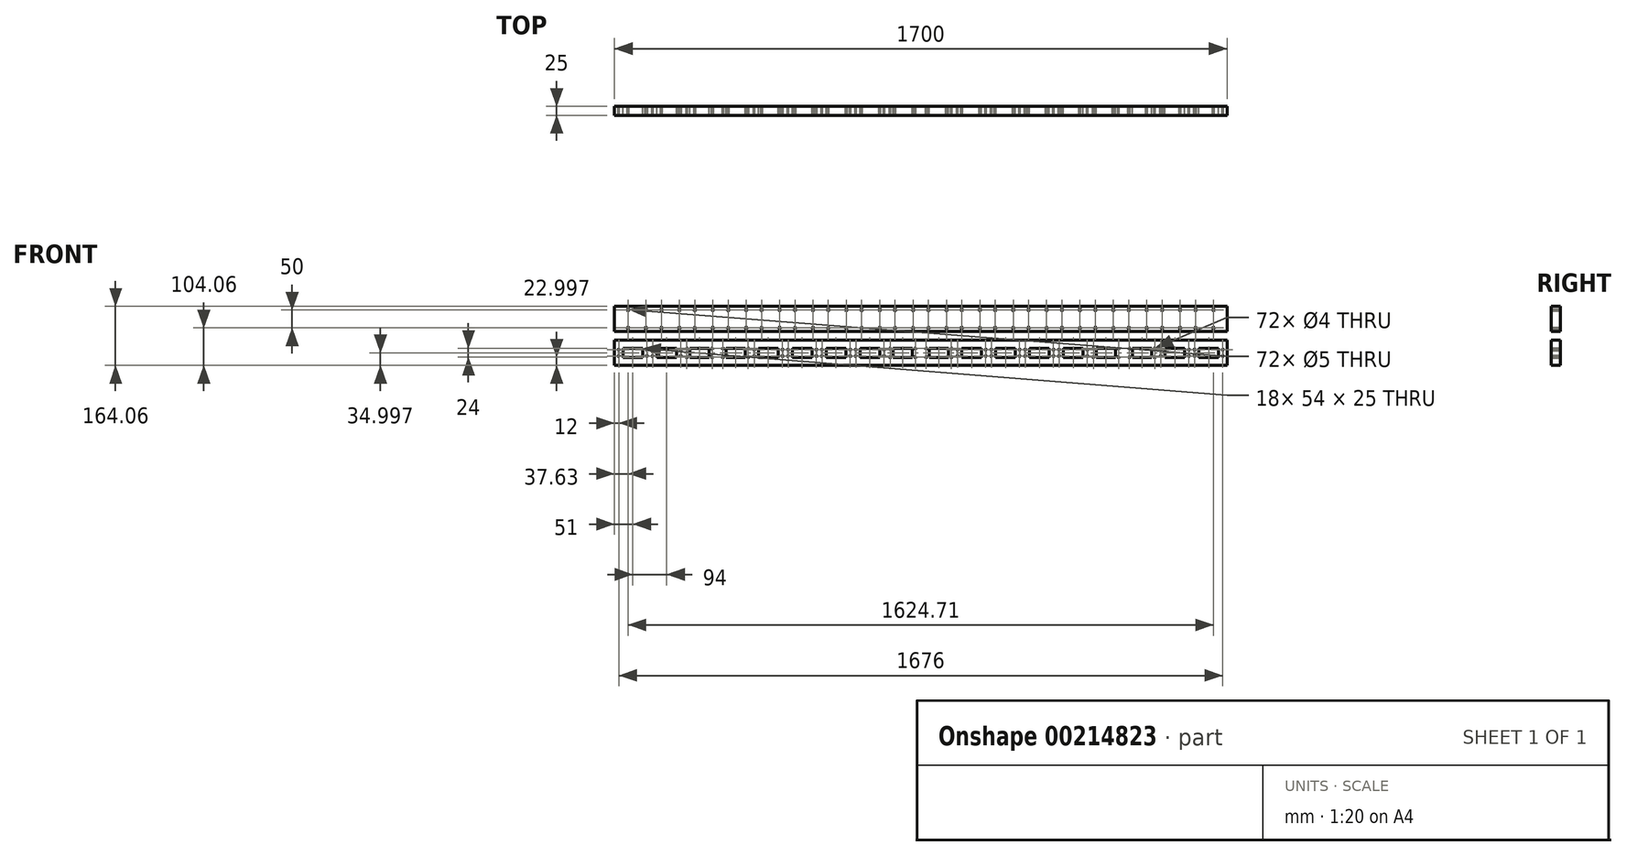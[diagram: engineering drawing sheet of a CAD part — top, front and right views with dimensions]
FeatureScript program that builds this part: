
annotation { "Feature Type Name" : "Feature", "Feature Type Description" : "" }
export const myFeature = defineFeature(function(context is Context, id is Id, definition is map)
    precondition{}
    {
        {
            var Q0;
            Q0=qCreatedBy(makeId("Front.planeOp"),FACE);
            var sketch = newSketch(context, id + "F0", { "sketchPlane" : qUnion([Q0])});
            skLineSegment(sketch, "E0.bottom", {"start": v(0, 0) * mm, "end": v(1700, 0) * mm});
            skLineSegment(sketch, "E0.top", {"start": v(0, 70) * mm, "end": v(1700, 70) * mm});
            skLineSegment(sketch, "E0.left", {"start": v(0, 0) * mm, "end": v(0, 70) * mm});
            skLineSegment(sketch, "E0.right", {"start": v(1700, 0) * mm, "end": v(1700, 70) * mm});
            skPoint(sketch, "E1.centerSnap0", {"position": v(0, 35) * mm});
            skCircle(sketch, "E2", {"center": v(37.63, 60) * mm, "radius": 2.5 * mm});
            skCircle(sketch, "E3.0.1.0", {"center": v(37.63, 10) * mm, "radius": 2.5 * mm});
            skCircle(sketch, "E3.1.0.0", {"center": v(87.63, 60) * mm, "radius": 2.5 * mm});
            skCircle(sketch, "E3.1.1.0", {"center": v(87.63, 10) * mm, "radius": 2.5 * mm});
            skLineSegment(sketch, "E3.direction1", {"start": v(37.63, 60) * mm, "end": v(87.63, 60) * mm, "construction": true});
            skLineSegment(sketch, "E3.direction2", {"start": v(37.63, 60) * mm, "end": v(37.63, 10) * mm, "construction": true});
            skCircle(sketch, "E4.1.0.0", {"center": v(130.26, 60) * mm, "radius": 2.5 * mm});
            skCircle(sketch, "E4.1.0.1", {"center": v(180.26, 60) * mm, "radius": 2.5 * mm});
            skCircle(sketch, "E4.1.0.2", {"center": v(180.26, 10) * mm, "radius": 2.5 * mm});
            skCircle(sketch, "E4.1.0.3", {"center": v(130.26, 10) * mm, "radius": 2.5 * mm});
            skCircle(sketch, "E4.2.0.0", {"center": v(222.89, 60) * mm, "radius": 2.5 * mm});
            skCircle(sketch, "E4.2.0.1", {"center": v(272.9, 60) * mm, "radius": 2.5 * mm});
            skCircle(sketch, "E4.2.0.2", {"center": v(272.9, 10) * mm, "radius": 2.5 * mm});
            skCircle(sketch, "E4.2.0.3", {"center": v(222.89, 10) * mm, "radius": 2.5 * mm});
            skCircle(sketch, "E4.3.0.0", {"center": v(315.52, 60) * mm, "radius": 2.5 * mm});
            skCircle(sketch, "E4.3.0.1", {"center": v(365.52, 60) * mm, "radius": 2.5 * mm});
            skCircle(sketch, "E4.3.0.2", {"center": v(365.52, 10) * mm, "radius": 2.5 * mm});
            skCircle(sketch, "E4.3.0.3", {"center": v(315.52, 10) * mm, "radius": 2.5 * mm});
            skCircle(sketch, "E4.4.0.0", {"center": v(408.15, 60) * mm, "radius": 2.5 * mm});
            skCircle(sketch, "E4.4.0.1", {"center": v(458.15, 60) * mm, "radius": 2.5 * mm});
            skCircle(sketch, "E4.4.0.2", {"center": v(458.15, 10) * mm, "radius": 2.5 * mm});
            skCircle(sketch, "E4.4.0.3", {"center": v(408.15, 10) * mm, "radius": 2.5 * mm});
            skCircle(sketch, "E4.5.0.0", {"center": v(500.78, 60) * mm, "radius": 2.5 * mm});
            skCircle(sketch, "E4.5.0.1", {"center": v(550.78, 60) * mm, "radius": 2.5 * mm});
            skCircle(sketch, "E4.5.0.2", {"center": v(550.78, 10) * mm, "radius": 2.5 * mm});
            skCircle(sketch, "E4.5.0.3", {"center": v(500.78, 10) * mm, "radius": 2.5 * mm});
            skCircle(sketch, "E4.6.0.0", {"center": v(593.4, 60) * mm, "radius": 2.5 * mm});
            skCircle(sketch, "E4.6.0.1", {"center": v(643.41, 60) * mm, "radius": 2.5 * mm});
            skCircle(sketch, "E4.6.0.2", {"center": v(643.41, 10) * mm, "radius": 2.5 * mm});
            skCircle(sketch, "E4.6.0.3", {"center": v(593.4, 10) * mm, "radius": 2.5 * mm});
            skCircle(sketch, "E4.7.0.0", {"center": v(686.04, 60) * mm, "radius": 2.5 * mm});
            skCircle(sketch, "E4.7.0.1", {"center": v(736.04, 60) * mm, "radius": 2.5 * mm});
            skCircle(sketch, "E4.7.0.2", {"center": v(736.04, 10) * mm, "radius": 2.5 * mm});
            skCircle(sketch, "E4.7.0.3", {"center": v(686.04, 10) * mm, "radius": 2.5 * mm});
            skCircle(sketch, "E4.8.0.0", {"center": v(778.67, 60) * mm, "radius": 2.5 * mm});
            skCircle(sketch, "E4.8.0.1", {"center": v(828.67, 60) * mm, "radius": 2.5 * mm});
            skCircle(sketch, "E4.8.0.2", {"center": v(828.67, 10) * mm, "radius": 2.5 * mm});
            skCircle(sketch, "E4.8.0.3", {"center": v(778.67, 10) * mm, "radius": 2.5 * mm});
            skCircle(sketch, "E4.9.0.0", {"center": v(871.3, 60) * mm, "radius": 2.5 * mm});
            skCircle(sketch, "E4.9.0.1", {"center": v(921.3, 60) * mm, "radius": 2.5 * mm});
            skCircle(sketch, "E4.9.0.2", {"center": v(921.3, 10) * mm, "radius": 2.5 * mm});
            skCircle(sketch, "E4.9.0.3", {"center": v(871.3, 10) * mm, "radius": 2.5 * mm});
            skLineSegment(sketch, "E4.direction1", {"start": v(37.63, 60) * mm, "end": v(130.26, 60) * mm, "construction": true});
            skCircle(sketch, "E5.0.10.0", {"center": v(963.93, 60) * mm, "radius": 2.5 * mm});
            skCircle(sketch, "E5.2.10.0", {"center": v(1013.93, 60) * mm, "radius": 2.5 * mm});
            skCircle(sketch, "E5.4.10.0", {"center": v(1013.93, 10) * mm, "radius": 2.5 * mm});
            skCircle(sketch, "E5.6.10.0", {"center": v(963.93, 10) * mm, "radius": 2.5 * mm});
            skCircle(sketch, "E5.0.11.0", {"center": v(1056.56, 60) * mm, "radius": 2.5 * mm});
            skCircle(sketch, "E5.2.11.0", {"center": v(1106.56, 60) * mm, "radius": 2.5 * mm});
            skCircle(sketch, "E5.4.11.0", {"center": v(1106.56, 10) * mm, "radius": 2.5 * mm});
            skCircle(sketch, "E5.6.11.0", {"center": v(1056.56, 10) * mm, "radius": 2.5 * mm});
            skCircle(sketch, "E5.0.12.0", {"center": v(1149.2, 60) * mm, "radius": 2.5 * mm});
            skCircle(sketch, "E5.2.12.0", {"center": v(1199.2, 60) * mm, "radius": 2.5 * mm});
            skCircle(sketch, "E5.4.12.0", {"center": v(1199.2, 10) * mm, "radius": 2.5 * mm});
            skCircle(sketch, "E5.6.12.0", {"center": v(1149.2, 10) * mm, "radius": 2.5 * mm});
            skCircle(sketch, "E5.0.13.0", {"center": v(1241.82, 60) * mm, "radius": 2.5 * mm});
            skCircle(sketch, "E5.2.13.0", {"center": v(1291.82, 60) * mm, "radius": 2.5 * mm});
            skCircle(sketch, "E5.4.13.0", {"center": v(1291.82, 10) * mm, "radius": 2.5 * mm});
            skCircle(sketch, "E5.6.13.0", {"center": v(1241.82, 10) * mm, "radius": 2.5 * mm});
            skCircle(sketch, "E5.0.14.0", {"center": v(1334.45, 60) * mm, "radius": 2.5 * mm});
            skCircle(sketch, "E5.2.14.0", {"center": v(1384.45, 60) * mm, "radius": 2.5 * mm});
            skCircle(sketch, "E5.4.14.0", {"center": v(1384.45, 10) * mm, "radius": 2.5 * mm});
            skCircle(sketch, "E5.6.14.0", {"center": v(1334.45, 10) * mm, "radius": 2.5 * mm});
            skCircle(sketch, "E5.0.15.0", {"center": v(1427.08, 60) * mm, "radius": 2.5 * mm});
            skCircle(sketch, "E5.2.15.0", {"center": v(1477.08, 60) * mm, "radius": 2.5 * mm});
            skCircle(sketch, "E5.4.15.0", {"center": v(1477.08, 10) * mm, "radius": 2.5 * mm});
            skCircle(sketch, "E5.6.15.0", {"center": v(1427.08, 10) * mm, "radius": 2.5 * mm});
            skCircle(sketch, "E5.0.16.0", {"center": v(1519.7, 60) * mm, "radius": 2.5 * mm});
            skCircle(sketch, "E5.2.16.0", {"center": v(1569.71, 60) * mm, "radius": 2.5 * mm});
            skCircle(sketch, "E5.4.16.0", {"center": v(1569.71, 10) * mm, "radius": 2.5 * mm});
            skCircle(sketch, "E5.6.16.0", {"center": v(1519.7, 10) * mm, "radius": 2.5 * mm});
            skCircle(sketch, "E5.0.17.0", {"center": v(1612.34, 60) * mm, "radius": 2.5 * mm});
            skCircle(sketch, "E5.2.17.0", {"center": v(1662.34, 60) * mm, "radius": 2.5 * mm});
            skCircle(sketch, "E5.4.17.0", {"center": v(1662.34, 10) * mm, "radius": 2.5 * mm});
            skCircle(sketch, "E5.6.17.0", {"center": v(1612.34, 10) * mm, "radius": 2.5 * mm});
            skSolve(sketch);
        }
        {
            var Q0;
            Q0=makeQuery(id+"F0.imprint","IMPRINT",FACE,{"disambiguationData":[TD([[makeQuery(id+"F0.imprint","IMPRINT",EDGE,{"derivedFrom":sQuery(id+"F0.wireOp",EDGE,"E0.bottom")}),1.0]])]});
            extrude(context, id + "F1", {"entities" : qUnion([Q0]), "depth" : 25 * mm});
        }
        {
            var Q0;
            Q0=qCreatedBy(makeId("Front.planeOp"),FACE);
            var sketch = newSketch(context, id + "F2", { "sketchPlane" : qUnion([Q0])});
            skLineSegment(sketch, "E6.bottom", {"start": v(0, -24.06) * mm, "end": v(1700, -24.06) * mm});
            skLineSegment(sketch, "E6.top", {"start": v(0, -94.06) * mm, "end": v(1700, -94.06) * mm});
            skLineSegment(sketch, "E6.left", {"start": v(0, -24.06) * mm, "end": v(0, -94.06) * mm});
            skLineSegment(sketch, "E6.right", {"start": v(1700, -24.06) * mm, "end": v(1700, -94.06) * mm});
            skLineSegment(sketch, "E7", {"start": v(0, -44.06) * mm, "end": v(1700, -44.06) * mm, "construction": true});
            skLineSegment(sketch, "E8.bottom", {"start": v(95, -46.06) * mm, "end": v(7, -46.06) * mm, "construction": true});
            skLineSegment(sketch, "E8.top", {"start": v(95, -72.06) * mm, "end": v(7, -72.06) * mm, "construction": true});
            skLineSegment(sketch, "E8.left", {"start": v(95, -46.06) * mm, "end": v(95, -72.06) * mm, "construction": true});
            skLineSegment(sketch, "E8.right", {"start": v(7, -46.06) * mm, "end": v(7, -72.06) * mm, "construction": true});
            skPoint(sketch, "E8.middle", {"position": v(51, -59.06) * mm});
            skPoint(sketch, "E8.middle.positionSnap0", {"position": v(0, -59.06) * mm});
            skPoint(sketch, "E8.centerSnap0", {"position": v(0, -59.06) * mm});
            skLineSegment(sketch, "E9.bottom", {"start": v(95, -46.06) * mm, "end": v(98, -46.06) * mm, "construction": true});
            skLineSegment(sketch, "E9.top", {"start": v(95, -72.06) * mm, "end": v(98, -72.06) * mm, "construction": true});
            skLineSegment(sketch, "E9.right", {"start": v(98, -46.06) * mm, "end": v(98, -72.06) * mm, "construction": true});
            skLineSegment(sketch, "E10.bottom", {"start": v(90, -50.31) * mm, "end": v(12, -50.31) * mm, "construction": true});
            skLineSegment(sketch, "E10.top", {"start": v(90, -67.81) * mm, "end": v(12, -67.81) * mm, "construction": true});
            skLineSegment(sketch, "E10.left", {"start": v(90, -50.31) * mm, "end": v(90, -67.81) * mm, "construction": true});
            skLineSegment(sketch, "E10.right", {"start": v(12, -50.31) * mm, "end": v(12, -67.81) * mm, "construction": true});
            skCircle(sketch, "E11", {"center": v(12, -50.31) * mm, "radius": 2 * mm});
            skCircle(sketch, "E12", {"center": v(90, -50.31) * mm, "radius": 2 * mm});
            skCircle(sketch, "E13", {"center": v(12, -67.81) * mm, "radius": 2 * mm});
            skCircle(sketch, "E14", {"center": v(90, -67.81) * mm, "radius": 2 * mm});
            skLineSegment(sketch, "E15.MirrorCS", {"start": v(101, -46.06) * mm, "end": v(98, -46.06) * mm, "construction": true});
            skLineSegment(sketch, "E16.MirrorCS", {"start": v(101, -72.06) * mm, "end": v(98, -72.06) * mm, "construction": true});
            skPoint(sketch, "E17.MirrorP", {"position": v(145, -59.06) * mm});
            skLineSegment(sketch, "E18.MirrorCS", {"start": v(101, -46.06) * mm, "end": v(189, -46.06) * mm, "construction": true});
            skLineSegment(sketch, "E19.MirrorCS", {"start": v(106, -50.31) * mm, "end": v(106, -67.81) * mm, "construction": true});
            skLineSegment(sketch, "E20.MirrorCS", {"start": v(184, -50.31) * mm, "end": v(184, -67.81) * mm, "construction": true});
            skCircle(sketch, "E21.MirrorC", {"center": v(184, -50.31) * mm, "radius": 2 * mm});
            skLineSegment(sketch, "E22.MirrorCS", {"start": v(189, -46.06) * mm, "end": v(189, -72.06) * mm, "construction": true});
            skLineSegment(sketch, "E23.MirrorCS", {"start": v(101, -46.06) * mm, "end": v(101, -72.06) * mm, "construction": true});
            skLineSegment(sketch, "E24.MirrorCS", {"start": v(106, -50.31) * mm, "end": v(184, -50.31) * mm, "construction": true});
            skCircle(sketch, "E25.MirrorC", {"center": v(106, -50.31) * mm, "radius": 2 * mm});
            skLineSegment(sketch, "E26.MirrorCS", {"start": v(101, -72.06) * mm, "end": v(189, -72.06) * mm, "construction": true});
            skLineSegment(sketch, "E27.MirrorCS", {"start": v(106, -67.81) * mm, "end": v(184, -67.81) * mm, "construction": true});
            skCircle(sketch, "E28.MirrorC", {"center": v(106, -67.81) * mm, "radius": 2 * mm});
            skCircle(sketch, "E29.MirrorC", {"center": v(184, -67.81) * mm, "radius": 2 * mm});
            skLineSegment(sketch, "E30.bottom", {"start": v(189, -41.56) * mm, "end": v(283, -41.56) * mm, "construction": true});
            skLineSegment(sketch, "E30.top", {"start": v(189, -76.56) * mm, "end": v(283, -76.56) * mm, "construction": true});
            skLineSegment(sketch, "E30.left", {"start": v(189, -41.56) * mm, "end": v(189, -76.56) * mm, "construction": true});
            skLineSegment(sketch, "E30.right", {"start": v(283, -41.56) * mm, "end": v(283, -76.56) * mm, "construction": true});
            skPoint(sketch, "E30.middle", {"position": v(236, -59.06) * mm});
            skLineSegment(sketch, "E31.bottom", {"start": v(283, -41.56) * mm, "end": v(286, -41.56) * mm, "construction": true});
            skLineSegment(sketch, "E31.top", {"start": v(283, -76.56) * mm, "end": v(286, -76.56) * mm, "construction": true});
            skLineSegment(sketch, "E31.right", {"start": v(286, -41.56) * mm, "end": v(286, -76.56) * mm, "construction": true});
            skLineSegment(sketch, "E32.bottom", {"start": v(271, -47.06) * mm, "end": v(201, -47.06) * mm, "construction": true});
            skLineSegment(sketch, "E32.top", {"start": v(271, -71.06) * mm, "end": v(201, -71.06) * mm, "construction": true});
            skLineSegment(sketch, "E32.left", {"start": v(271, -47.06) * mm, "end": v(271, -71.06) * mm, "construction": true});
            skLineSegment(sketch, "E32.right", {"start": v(201, -47.06) * mm, "end": v(201, -71.06) * mm, "construction": true});
            skCircle(sketch, "E33", {"center": v(201, -47.06) * mm, "radius": 2 * mm});
            skCircle(sketch, "E34", {"center": v(271, -47.06) * mm, "radius": 2 * mm});
            skCircle(sketch, "E35", {"center": v(271, -71.06) * mm, "radius": 2 * mm});
            skCircle(sketch, "E36", {"center": v(201, -71.06) * mm, "radius": 2 * mm});
            skLineSegment(sketch, "E37.bottom", {"start": v(78, -46.56) * mm, "end": v(24, -46.56) * mm});
            skLineSegment(sketch, "E37.top", {"start": v(78, -71.56) * mm, "end": v(24, -71.56) * mm});
            skLineSegment(sketch, "E37.left", {"start": v(78, -46.56) * mm, "end": v(78, -71.56) * mm});
            skLineSegment(sketch, "E37.right", {"start": v(24, -46.56) * mm, "end": v(24, -71.56) * mm});
            skLineSegment(sketch, "E38.bottom", {"start": v(172, -46.56) * mm, "end": v(118, -46.56) * mm});
            skLineSegment(sketch, "E38.top", {"start": v(172, -71.56) * mm, "end": v(118, -71.56) * mm});
            skLineSegment(sketch, "E38.left", {"start": v(172, -46.56) * mm, "end": v(172, -71.56) * mm});
            skLineSegment(sketch, "E38.right", {"start": v(118, -46.56) * mm, "end": v(118, -71.56) * mm});
            skLineSegment(sketch, "E39.bottom", {"start": v(263, -46.56) * mm, "end": v(209, -46.56) * mm});
            skLineSegment(sketch, "E39.top", {"start": v(263, -71.56) * mm, "end": v(209, -71.56) * mm});
            skLineSegment(sketch, "E39.left", {"start": v(263, -46.56) * mm, "end": v(263, -71.56) * mm});
            skLineSegment(sketch, "E39.right", {"start": v(209, -46.56) * mm, "end": v(209, -71.56) * mm});
            skLineSegment(sketch, "E40.MirrorCS", {"start": v(471, -72.06) * mm, "end": v(474, -72.06) * mm, "construction": true});
            skLineSegment(sketch, "E41.MirrorCS", {"start": v(477, -72.06) * mm, "end": v(474, -72.06) * mm, "construction": true});
            skLineSegment(sketch, "E42.MirrorCS", {"start": v(289, -41.56) * mm, "end": v(286, -41.56) * mm, "construction": true});
            skLineSegment(sketch, "E43.MirrorCS", {"start": v(289, -76.56) * mm, "end": v(286, -76.56) * mm, "construction": true});
            skCircle(sketch, "E44.MirrorC", {"center": v(388, -67.81) * mm, "radius": 2 * mm});
            skCircle(sketch, "E45.MirrorC", {"center": v(482, -50.31) * mm, "radius": 2 * mm});
            skCircle(sketch, "E46.MirrorC", {"center": v(371, -71.06) * mm, "radius": 2 * mm});
            skCircle(sketch, "E47.MirrorC", {"center": v(301, -47.06) * mm, "radius": 2 * mm});
            skCircle(sketch, "E48.MirrorC", {"center": v(466, -50.31) * mm, "radius": 2 * mm});
            skLineSegment(sketch, "E49.MirrorCS", {"start": v(471, -46.06) * mm, "end": v(474, -46.06) * mm, "construction": true});
            skCircle(sketch, "E50.MirrorC", {"center": v(388, -50.31) * mm, "radius": 2 * mm});
            skCircle(sketch, "E51.MirrorC", {"center": v(466, -67.81) * mm, "radius": 2 * mm});
            skCircle(sketch, "E52.MirrorC", {"center": v(560, -67.81) * mm, "radius": 2 * mm});
            skCircle(sketch, "E53.MirrorC", {"center": v(371, -47.06) * mm, "radius": 2 * mm});
            skLineSegment(sketch, "E54.MirrorCS", {"start": v(477, -46.06) * mm, "end": v(474, -46.06) * mm, "construction": true});
            skCircle(sketch, "E55.MirrorC", {"center": v(301, -71.06) * mm, "radius": 2 * mm});
            skCircle(sketch, "E56.MirrorC", {"center": v(482, -67.81) * mm, "radius": 2 * mm});
            skCircle(sketch, "E57.MirrorC", {"center": v(560, -50.31) * mm, "radius": 2 * mm});
            skPoint(sketch, "E58.MirrorP", {"position": v(427, -59.06) * mm});
            skPoint(sketch, "E59.MirrorP", {"position": v(521, -59.06) * mm});
            skPoint(sketch, "E60.MirrorP", {"position": v(336, -59.06) * mm});
            skLineSegment(sketch, "E61.MirrorCS", {"start": v(289, -41.56) * mm, "end": v(289, -76.56) * mm, "construction": true});
            skLineSegment(sketch, "E62.MirrorCS", {"start": v(383, -41.56) * mm, "end": v(383, -76.56) * mm, "construction": true});
            skLineSegment(sketch, "E63.MirrorCS", {"start": v(309, -71.56) * mm, "end": v(363, -71.56) * mm});
            skLineSegment(sketch, "E64.MirrorCS", {"start": v(400, -71.56) * mm, "end": v(454, -71.56) * mm});
            skLineSegment(sketch, "E65.MirrorCS", {"start": v(494, -71.56) * mm, "end": v(548, -71.56) * mm});
            skLineSegment(sketch, "E66.MirrorCS", {"start": v(309, -46.56) * mm, "end": v(363, -46.56) * mm});
            skLineSegment(sketch, "E67.MirrorCS", {"start": v(388, -50.31) * mm, "end": v(388, -67.81) * mm, "construction": true});
            skLineSegment(sketch, "E68.MirrorCS", {"start": v(471, -72.06) * mm, "end": v(383, -72.06) * mm, "construction": true});
            skLineSegment(sketch, "E69.MirrorCS", {"start": v(548, -46.56) * mm, "end": v(548, -71.56) * mm});
            skLineSegment(sketch, "E70.MirrorCS", {"start": v(482, -67.81) * mm, "end": v(560, -67.81) * mm, "construction": true});
            skLineSegment(sketch, "E71.MirrorCS", {"start": v(474, -46.06) * mm, "end": v(474, -72.06) * mm, "construction": true});
            skLineSegment(sketch, "E72.MirrorCS", {"start": v(471, -46.06) * mm, "end": v(383, -46.06) * mm, "construction": true});
            skLineSegment(sketch, "E73.MirrorCS", {"start": v(466, -67.81) * mm, "end": v(388, -67.81) * mm, "construction": true});
            skLineSegment(sketch, "E74.MirrorCS", {"start": v(466, -50.31) * mm, "end": v(388, -50.31) * mm, "construction": true});
            skLineSegment(sketch, "E75.MirrorCS", {"start": v(400, -46.56) * mm, "end": v(400, -71.56) * mm});
            skLineSegment(sketch, "E76.MirrorCS", {"start": v(383, -46.06) * mm, "end": v(383, -72.06) * mm, "construction": true});
            skLineSegment(sketch, "E77.MirrorCS", {"start": v(565, -46.06) * mm, "end": v(565, -72.06) * mm, "construction": true});
            skLineSegment(sketch, "E78.MirrorCS", {"start": v(363, -46.56) * mm, "end": v(363, -71.56) * mm});
            skLineSegment(sketch, "E79.MirrorCS", {"start": v(371, -47.06) * mm, "end": v(371, -71.06) * mm, "construction": true});
            skLineSegment(sketch, "E80.MirrorCS", {"start": v(383, -41.56) * mm, "end": v(289, -41.56) * mm, "construction": true});
            skLineSegment(sketch, "E81.MirrorCS", {"start": v(482, -50.31) * mm, "end": v(482, -67.81) * mm, "construction": true});
            skLineSegment(sketch, "E82.MirrorCS", {"start": v(477, -46.06) * mm, "end": v(565, -46.06) * mm, "construction": true});
            skLineSegment(sketch, "E83.MirrorCS", {"start": v(400, -46.56) * mm, "end": v(454, -46.56) * mm});
            skLineSegment(sketch, "E84.MirrorCS", {"start": v(494, -46.56) * mm, "end": v(548, -46.56) * mm});
            skLineSegment(sketch, "E85.MirrorCS", {"start": v(309, -46.56) * mm, "end": v(309, -71.56) * mm});
            skLineSegment(sketch, "E86.MirrorCS", {"start": v(301, -47.06) * mm, "end": v(301, -71.06) * mm, "construction": true});
            skLineSegment(sketch, "E87.MirrorCS", {"start": v(560, -50.31) * mm, "end": v(560, -67.81) * mm, "construction": true});
            skLineSegment(sketch, "E88.MirrorCS", {"start": v(301, -71.06) * mm, "end": v(371, -71.06) * mm, "construction": true});
            skLineSegment(sketch, "E89.MirrorCS", {"start": v(471, -46.06) * mm, "end": v(471, -72.06) * mm, "construction": true});
            skLineSegment(sketch, "E90.MirrorCS", {"start": v(466, -50.31) * mm, "end": v(466, -67.81) * mm, "construction": true});
            skLineSegment(sketch, "E91.MirrorCS", {"start": v(383, -76.56) * mm, "end": v(289, -76.56) * mm, "construction": true});
            skLineSegment(sketch, "E92.MirrorCS", {"start": v(477, -72.06) * mm, "end": v(565, -72.06) * mm, "construction": true});
            skLineSegment(sketch, "E93.MirrorCS", {"start": v(301, -47.06) * mm, "end": v(371, -47.06) * mm, "construction": true});
            skLineSegment(sketch, "E94.MirrorCS", {"start": v(477, -46.06) * mm, "end": v(477, -72.06) * mm, "construction": true});
            skLineSegment(sketch, "E95.MirrorCS", {"start": v(454, -46.56) * mm, "end": v(454, -71.56) * mm});
            skLineSegment(sketch, "E96.MirrorCS", {"start": v(482, -50.31) * mm, "end": v(560, -50.31) * mm, "construction": true});
            skLineSegment(sketch, "E97.MirrorCS", {"start": v(494, -46.56) * mm, "end": v(494, -71.56) * mm});
            skLineSegment(sketch, "E98.1.0.0", {"start": v(1124, -50.31) * mm, "end": v(1124, -67.81) * mm, "construction": true});
            skLineSegment(sketch, "E98.1.0.1", {"start": v(1038, -46.06) * mm, "end": v(1038, -72.06) * mm, "construction": true});
            skLineSegment(sketch, "E98.1.0.2", {"start": v(1030, -67.81) * mm, "end": v(952, -67.81) * mm, "construction": true});
            skLineSegment(sketch, "E98.1.0.3", {"start": v(947, -41.56) * mm, "end": v(853, -41.56) * mm, "construction": true});
            skLineSegment(sketch, "E98.1.0.4", {"start": v(642, -46.56) * mm, "end": v(642, -71.56) * mm});
            skLineSegment(sketch, "E98.1.0.5", {"start": v(765, -47.06) * mm, "end": v(765, -71.06) * mm, "construction": true});
            skLineSegment(sketch, "E98.1.0.6", {"start": v(773, -46.56) * mm, "end": v(773, -71.56) * mm});
            skLineSegment(sketch, "E98.1.0.7", {"start": v(665, -46.06) * mm, "end": v(665, -72.06) * mm, "construction": true});
            skLineSegment(sketch, "E98.1.0.8", {"start": v(835, -71.06) * mm, "end": v(765, -71.06) * mm, "construction": true});
            skLineSegment(sketch, "E98.1.0.9", {"start": v(1035, -46.06) * mm, "end": v(1035, -72.06) * mm, "construction": true});
            skLineSegment(sketch, "E98.1.0.10", {"start": v(1046, -50.31) * mm, "end": v(1124, -50.31) * mm, "construction": true});
            skLineSegment(sketch, "E98.1.0.11", {"start": v(827, -46.56) * mm, "end": v(827, -71.56) * mm});
            skLineSegment(sketch, "E98.1.0.12", {"start": v(835, -47.06) * mm, "end": v(835, -71.06) * mm, "construction": true});
            skLineSegment(sketch, "E98.1.0.13", {"start": v(670, -50.31) * mm, "end": v(748, -50.31) * mm, "construction": true});
            skLineSegment(sketch, "E98.1.0.14", {"start": v(865, -71.06) * mm, "end": v(935, -71.06) * mm, "construction": true});
            skLineSegment(sketch, "E98.1.0.15", {"start": v(1035, -46.06) * mm, "end": v(947, -46.06) * mm, "construction": true});
            skLineSegment(sketch, "E98.1.0.16", {"start": v(665, -72.06) * mm, "end": v(753, -72.06) * mm, "construction": true});
            skLineSegment(sketch, "E98.1.0.17", {"start": v(1046, -50.31) * mm, "end": v(1046, -67.81) * mm, "construction": true});
            skLineSegment(sketch, "E98.1.0.18", {"start": v(935, -47.06) * mm, "end": v(935, -71.06) * mm, "construction": true});
            skLineSegment(sketch, "E98.1.0.19", {"start": v(847, -41.56) * mm, "end": v(847, -76.56) * mm, "construction": true});
            skLineSegment(sketch, "E98.1.0.20", {"start": v(1046, -67.81) * mm, "end": v(1124, -67.81) * mm, "construction": true});
            skLineSegment(sketch, "E98.1.0.21", {"start": v(659, -46.06) * mm, "end": v(659, -72.06) * mm, "construction": true});
            skLineSegment(sketch, "E98.1.0.22", {"start": v(753, -46.06) * mm, "end": v(753, -72.06) * mm, "construction": true});
            skLineSegment(sketch, "E98.1.0.23", {"start": v(1058, -46.56) * mm, "end": v(1058, -71.56) * mm});
            skLineSegment(sketch, "E98.1.0.24", {"start": v(927, -46.56) * mm, "end": v(927, -71.56) * mm});
            skLineSegment(sketch, "E98.1.0.25", {"start": v(659, -72.06) * mm, "end": v(571, -72.06) * mm, "construction": true});
            skLineSegment(sketch, "E98.1.0.26", {"start": v(1030, -50.31) * mm, "end": v(1030, -67.81) * mm, "construction": true});
            skLineSegment(sketch, "E98.1.0.27", {"start": v(1035, -72.06) * mm, "end": v(947, -72.06) * mm, "construction": true});
            skLineSegment(sketch, "E98.1.0.28", {"start": v(659, -46.06) * mm, "end": v(571, -46.06) * mm, "construction": true});
            skPoint(sketch, "E98.1.0.29", {"position": v(709, -59.06) * mm});
            skLineSegment(sketch, "E98.1.0.30", {"start": v(1018, -46.56) * mm, "end": v(1018, -71.56) * mm});
            skLineSegment(sketch, "E98.1.0.31", {"start": v(670, -50.31) * mm, "end": v(670, -67.81) * mm, "construction": true});
            skLineSegment(sketch, "E98.1.0.32", {"start": v(1041, -72.06) * mm, "end": v(1129, -72.06) * mm, "construction": true});
            skPoint(sketch, "E98.1.0.33", {"position": v(1085, -59.06) * mm});
            skLineSegment(sketch, "E98.1.0.34", {"start": v(1041, -46.06) * mm, "end": v(1129, -46.06) * mm, "construction": true});
            skLineSegment(sketch, "E98.1.0.35", {"start": v(964, -46.56) * mm, "end": v(964, -71.56) * mm});
            skLineSegment(sketch, "E98.1.0.36", {"start": v(670, -67.81) * mm, "end": v(748, -67.81) * mm, "construction": true});
            skLineSegment(sketch, "E98.1.0.37", {"start": v(588, -46.56) * mm, "end": v(588, -71.56) * mm});
            skLineSegment(sketch, "E98.1.0.38", {"start": v(654, -50.31) * mm, "end": v(576, -50.31) * mm, "construction": true});
            skLineSegment(sketch, "E98.1.0.39", {"start": v(850, -41.56) * mm, "end": v(850, -76.56) * mm, "construction": true});
            skLineSegment(sketch, "E98.1.0.40", {"start": v(654, -67.81) * mm, "end": v(576, -67.81) * mm, "construction": true});
            skLineSegment(sketch, "E98.1.0.41", {"start": v(1030, -50.31) * mm, "end": v(952, -50.31) * mm, "construction": true});
            skPoint(sketch, "E98.1.0.42", {"position": v(800, -59.06) * mm});
            skLineSegment(sketch, "E98.1.0.43", {"start": v(748, -50.31) * mm, "end": v(748, -67.81) * mm, "construction": true});
            skLineSegment(sketch, "E98.1.0.44", {"start": v(753, -76.56) * mm, "end": v(847, -76.56) * mm, "construction": true});
            skLineSegment(sketch, "E98.1.0.45", {"start": v(865, -47.06) * mm, "end": v(865, -71.06) * mm, "construction": true});
            skPoint(sketch, "E98.1.0.46", {"position": v(991, -59.06) * mm});
            skLineSegment(sketch, "E98.1.0.47", {"start": v(865, -47.06) * mm, "end": v(935, -47.06) * mm, "construction": true});
            skPoint(sketch, "E98.1.0.48", {"position": v(900, -59.06) * mm});
            skPoint(sketch, "E98.1.0.49", {"position": v(615, -59.06) * mm});
            skLineSegment(sketch, "E98.1.0.50", {"start": v(835, -47.06) * mm, "end": v(765, -47.06) * mm, "construction": true});
            skLineSegment(sketch, "E98.1.0.51", {"start": v(1041, -46.06) * mm, "end": v(1041, -72.06) * mm, "construction": true});
            skLineSegment(sketch, "E98.1.0.52", {"start": v(753, -41.56) * mm, "end": v(847, -41.56) * mm, "construction": true});
            skLineSegment(sketch, "E98.1.0.53", {"start": v(947, -76.56) * mm, "end": v(853, -76.56) * mm, "construction": true});
            skLineSegment(sketch, "E98.1.0.54", {"start": v(576, -50.31) * mm, "end": v(576, -67.81) * mm, "construction": true});
            skLineSegment(sketch, "E98.1.0.55", {"start": v(952, -50.31) * mm, "end": v(952, -67.81) * mm, "construction": true});
            skLineSegment(sketch, "E98.1.0.56", {"start": v(654, -50.31) * mm, "end": v(654, -67.81) * mm, "construction": true});
            skLineSegment(sketch, "E98.1.0.57", {"start": v(665, -46.06) * mm, "end": v(753, -46.06) * mm, "construction": true});
            skLineSegment(sketch, "E98.1.0.58", {"start": v(873, -46.56) * mm, "end": v(873, -71.56) * mm});
            skLineSegment(sketch, "E98.1.0.59", {"start": v(1112, -46.56) * mm, "end": v(1112, -71.56) * mm});
            skLineSegment(sketch, "E98.1.0.60", {"start": v(1129, -46.06) * mm, "end": v(1129, -72.06) * mm, "construction": true});
            skLineSegment(sketch, "E98.1.0.61", {"start": v(947, -41.56) * mm, "end": v(947, -76.56) * mm, "construction": true});
            skLineSegment(sketch, "E98.1.0.62", {"start": v(682, -46.56) * mm, "end": v(682, -71.56) * mm});
            skLineSegment(sketch, "E98.1.0.63", {"start": v(853, -41.56) * mm, "end": v(853, -76.56) * mm, "construction": true});
            skLineSegment(sketch, "E98.1.0.64", {"start": v(662, -46.06) * mm, "end": v(662, -72.06) * mm, "construction": true});
            skLineSegment(sketch, "E98.1.0.65", {"start": v(753, -41.56) * mm, "end": v(753, -76.56) * mm, "construction": true});
            skLineSegment(sketch, "E98.1.0.66", {"start": v(1058, -71.56) * mm, "end": v(1112, -71.56) * mm});
            skPoint(sketch, "E98.1.0.67", {"position": v(564, -59.06) * mm});
            skLineSegment(sketch, "E98.1.0.68", {"start": v(847, -41.56) * mm, "end": v(847, -76.56) * mm, "construction": true});
            skPoint(sketch, "E98.1.0.69", {"position": v(709, -59.06) * mm});
            skPoint(sketch, "E98.1.0.70", {"position": v(900, -59.06) * mm});
            skLineSegment(sketch, "E98.1.0.71", {"start": v(642, -71.56) * mm, "end": v(588, -71.56) * mm});
            skLineSegment(sketch, "E98.1.0.72", {"start": v(1058, -46.56) * mm, "end": v(1112, -46.56) * mm});
            skLineSegment(sketch, "E98.1.0.73", {"start": v(827, -71.56) * mm, "end": v(773, -71.56) * mm});
            skLineSegment(sketch, "E98.1.0.74", {"start": v(964, -46.56) * mm, "end": v(1018, -46.56) * mm});
            skPoint(sketch, "E98.1.0.75", {"position": v(1085, -59.06) * mm});
            skPoint(sketch, "E98.1.0.76", {"position": v(991, -59.06) * mm});
            skLineSegment(sketch, "E98.1.0.77", {"start": v(853, -41.56) * mm, "end": v(853, -76.56) * mm, "construction": true});
            skLineSegment(sketch, "E98.1.0.78", {"start": v(947, -46.06) * mm, "end": v(947, -72.06) * mm, "construction": true});
            skLineSegment(sketch, "E98.1.0.79", {"start": v(873, -46.56) * mm, "end": v(927, -46.56) * mm});
            skLineSegment(sketch, "E98.1.0.80", {"start": v(964, -71.56) * mm, "end": v(1018, -71.56) * mm});
            skLineSegment(sketch, "E98.1.0.81", {"start": v(736, -46.56) * mm, "end": v(736, -71.56) * mm});
            skLineSegment(sketch, "E98.1.0.82", {"start": v(873, -71.56) * mm, "end": v(927, -71.56) * mm});
            skLineSegment(sketch, "E98.1.0.83", {"start": v(736, -71.56) * mm, "end": v(682, -71.56) * mm});
            skLineSegment(sketch, "E98.1.0.84", {"start": v(827, -46.56) * mm, "end": v(773, -46.56) * mm});
            skLineSegment(sketch, "E98.1.0.85", {"start": v(642, -46.56) * mm, "end": v(588, -46.56) * mm});
            skLineSegment(sketch, "E98.1.0.86", {"start": v(736, -46.56) * mm, "end": v(682, -46.56) * mm});
            skPoint(sketch, "E98.1.0.87", {"position": v(800, -59.06) * mm});
            skPoint(sketch, "E98.1.0.88", {"position": v(615, -59.06) * mm});
            skPoint(sketch, "E98.1.0.89", {"position": v(800, -59.06) * mm});
            skPoint(sketch, "E98.1.0.90", {"position": v(1085, -59.06) * mm});
            skLineSegment(sketch, "E98.1.0.91", {"start": v(571, -46.06) * mm, "end": v(571, -72.06) * mm, "construction": true});
            skPoint(sketch, "E98.1.0.92", {"position": v(709, -59.06) * mm});
            skPoint(sketch, "E98.1.0.93", {"position": v(615, -59.06) * mm});
            skPoint(sketch, "E98.1.0.94", {"position": v(900, -59.06) * mm});
            skPoint(sketch, "E98.1.0.95", {"position": v(991, -59.06) * mm});
            skLineSegment(sketch, "E98.1.0.96", {"start": v(665, -46.06) * mm, "end": v(662, -46.06) * mm, "construction": true});
            skCircle(sketch, "E98.1.0.97", {"center": v(670, -50.31) * mm, "radius": 2 * mm});
            skCircle(sketch, "E98.1.0.98", {"center": v(865, -71.06) * mm, "radius": 2 * mm});
            skCircle(sketch, "E98.1.0.99", {"center": v(935, -71.06) * mm, "radius": 2 * mm});
            skLineSegment(sketch, "E98.1.0.100", {"start": v(1041, -46.06) * mm, "end": v(1038, -46.06) * mm, "construction": true});
            skCircle(sketch, "E98.1.0.101", {"center": v(748, -67.81) * mm, "radius": 2 * mm});
            skCircle(sketch, "E98.1.0.102", {"center": v(1046, -67.81) * mm, "radius": 2 * mm});
            skLineSegment(sketch, "E98.1.0.103", {"start": v(659, -46.06) * mm, "end": v(662, -46.06) * mm, "construction": true});
            skCircle(sketch, "E98.1.0.104", {"center": v(654, -67.81) * mm, "radius": 2 * mm});
            skCircle(sketch, "E98.1.0.105", {"center": v(952, -50.31) * mm, "radius": 2 * mm});
            skCircle(sketch, "E98.1.0.106", {"center": v(576, -67.81) * mm, "radius": 2 * mm});
            skCircle(sketch, "E98.1.0.107", {"center": v(654, -50.31) * mm, "radius": 2 * mm});
            skCircle(sketch, "E98.1.0.108", {"center": v(670, -67.81) * mm, "radius": 2 * mm});
            skCircle(sketch, "E98.1.0.109", {"center": v(1030, -50.31) * mm, "radius": 2 * mm});
            skCircle(sketch, "E98.1.0.110", {"center": v(765, -71.06) * mm, "radius": 2 * mm});
            skCircle(sketch, "E98.1.0.111", {"center": v(765, -47.06) * mm, "radius": 2 * mm});
            skCircle(sketch, "E98.1.0.112", {"center": v(865, -47.06) * mm, "radius": 2 * mm});
            skCircle(sketch, "E98.1.0.113", {"center": v(1046, -50.31) * mm, "radius": 2 * mm});
            skCircle(sketch, "E98.1.0.114", {"center": v(952, -67.81) * mm, "radius": 2 * mm});
            skCircle(sketch, "E98.1.0.115", {"center": v(1030, -67.81) * mm, "radius": 2 * mm});
            skCircle(sketch, "E98.1.0.116", {"center": v(576, -50.31) * mm, "radius": 2 * mm});
            skLineSegment(sketch, "E98.1.0.117", {"start": v(1035, -46.06) * mm, "end": v(1038, -46.06) * mm, "construction": true});
            skCircle(sketch, "E98.1.0.118", {"center": v(1124, -67.81) * mm, "radius": 2 * mm});
            skCircle(sketch, "E98.1.0.119", {"center": v(835, -71.06) * mm, "radius": 2 * mm});
            skCircle(sketch, "E98.1.0.120", {"center": v(835, -47.06) * mm, "radius": 2 * mm});
            skCircle(sketch, "E98.1.0.121", {"center": v(935, -47.06) * mm, "radius": 2 * mm});
            skCircle(sketch, "E98.1.0.122", {"center": v(1124, -50.31) * mm, "radius": 2 * mm});
            skCircle(sketch, "E98.1.0.123", {"center": v(748, -50.31) * mm, "radius": 2 * mm});
            skLineSegment(sketch, "E98.1.0.124", {"start": v(665, -72.06) * mm, "end": v(662, -72.06) * mm, "construction": true});
            skLineSegment(sketch, "E98.1.0.125", {"start": v(1035, -72.06) * mm, "end": v(1038, -72.06) * mm, "construction": true});
            skLineSegment(sketch, "E98.1.0.126", {"start": v(853, -41.56) * mm, "end": v(850, -41.56) * mm, "construction": true});
            skLineSegment(sketch, "E98.1.0.127", {"start": v(1041, -72.06) * mm, "end": v(1038, -72.06) * mm, "construction": true});
            skLineSegment(sketch, "E98.1.0.128", {"start": v(853, -76.56) * mm, "end": v(850, -76.56) * mm, "construction": true});
            skLineSegment(sketch, "E98.1.0.129", {"start": v(659, -72.06) * mm, "end": v(662, -72.06) * mm, "construction": true});
            skLineSegment(sketch, "E98.1.0.130", {"start": v(847, -76.56) * mm, "end": v(850, -76.56) * mm, "construction": true});
            skLineSegment(sketch, "E98.1.0.131", {"start": v(847, -41.56) * mm, "end": v(850, -41.56) * mm, "construction": true});
            skLineSegment(sketch, "E98.2.0.0", {"start": v(1688, -50.31) * mm, "end": v(1688, -67.81) * mm, "construction": true});
            skLineSegment(sketch, "E98.2.0.1", {"start": v(1602, -46.06) * mm, "end": v(1602, -72.06) * mm, "construction": true});
            skLineSegment(sketch, "E98.2.0.2", {"start": v(1594, -67.81) * mm, "end": v(1516, -67.81) * mm, "construction": true});
            skLineSegment(sketch, "E98.2.0.3", {"start": v(1511, -41.56) * mm, "end": v(1417, -41.56) * mm, "construction": true});
            skLineSegment(sketch, "E98.2.0.4", {"start": v(1206, -46.56) * mm, "end": v(1206, -71.56) * mm});
            skLineSegment(sketch, "E98.2.0.5", {"start": v(1329, -47.06) * mm, "end": v(1329, -71.06) * mm, "construction": true});
            skLineSegment(sketch, "E98.2.0.6", {"start": v(1337, -46.56) * mm, "end": v(1337, -71.56) * mm});
            skLineSegment(sketch, "E98.2.0.7", {"start": v(1229, -46.06) * mm, "end": v(1229, -72.06) * mm, "construction": true});
            skLineSegment(sketch, "E98.2.0.8", {"start": v(1399, -71.06) * mm, "end": v(1329, -71.06) * mm, "construction": true});
            skLineSegment(sketch, "E98.2.0.9", {"start": v(1599, -46.06) * mm, "end": v(1599, -72.06) * mm, "construction": true});
            skLineSegment(sketch, "E98.2.0.10", {"start": v(1610, -50.31) * mm, "end": v(1688, -50.31) * mm, "construction": true});
            skLineSegment(sketch, "E98.2.0.11", {"start": v(1391, -46.56) * mm, "end": v(1391, -71.56) * mm});
            skLineSegment(sketch, "E98.2.0.12", {"start": v(1399, -47.06) * mm, "end": v(1399, -71.06) * mm, "construction": true});
            skLineSegment(sketch, "E98.2.0.13", {"start": v(1234, -50.31) * mm, "end": v(1312, -50.31) * mm, "construction": true});
            skLineSegment(sketch, "E98.2.0.14", {"start": v(1429, -71.06) * mm, "end": v(1499, -71.06) * mm, "construction": true});
            skLineSegment(sketch, "E98.2.0.15", {"start": v(1599, -46.06) * mm, "end": v(1511, -46.06) * mm, "construction": true});
            skLineSegment(sketch, "E98.2.0.16", {"start": v(1229, -72.06) * mm, "end": v(1317, -72.06) * mm, "construction": true});
            skLineSegment(sketch, "E98.2.0.17", {"start": v(1610, -50.31) * mm, "end": v(1610, -67.81) * mm, "construction": true});
            skLineSegment(sketch, "E98.2.0.18", {"start": v(1499, -47.06) * mm, "end": v(1499, -71.06) * mm, "construction": true});
            skLineSegment(sketch, "E98.2.0.19", {"start": v(1411, -41.56) * mm, "end": v(1411, -76.56) * mm, "construction": true});
            skLineSegment(sketch, "E98.2.0.20", {"start": v(1610, -67.81) * mm, "end": v(1688, -67.81) * mm, "construction": true});
            skLineSegment(sketch, "E98.2.0.21", {"start": v(1223, -46.06) * mm, "end": v(1223, -72.06) * mm, "construction": true});
            skLineSegment(sketch, "E98.2.0.22", {"start": v(1317, -46.06) * mm, "end": v(1317, -72.06) * mm, "construction": true});
            skLineSegment(sketch, "E98.2.0.23", {"start": v(1622, -46.56) * mm, "end": v(1622, -71.56) * mm});
            skLineSegment(sketch, "E98.2.0.24", {"start": v(1491, -46.56) * mm, "end": v(1491, -71.56) * mm});
            skLineSegment(sketch, "E98.2.0.25", {"start": v(1223, -72.06) * mm, "end": v(1135, -72.06) * mm, "construction": true});
            skLineSegment(sketch, "E98.2.0.26", {"start": v(1594, -50.31) * mm, "end": v(1594, -67.81) * mm, "construction": true});
            skLineSegment(sketch, "E98.2.0.27", {"start": v(1599, -72.06) * mm, "end": v(1511, -72.06) * mm, "construction": true});
            skLineSegment(sketch, "E98.2.0.28", {"start": v(1223, -46.06) * mm, "end": v(1135, -46.06) * mm, "construction": true});
            skPoint(sketch, "E98.2.0.29", {"position": v(1273, -59.06) * mm});
            skLineSegment(sketch, "E98.2.0.30", {"start": v(1582, -46.56) * mm, "end": v(1582, -71.56) * mm});
            skLineSegment(sketch, "E98.2.0.31", {"start": v(1234, -50.31) * mm, "end": v(1234, -67.81) * mm, "construction": true});
            skLineSegment(sketch, "E98.2.0.32", {"start": v(1605, -72.06) * mm, "end": v(1693, -72.06) * mm, "construction": true});
            skPoint(sketch, "E98.2.0.33", {"position": v(1649, -59.06) * mm});
            skLineSegment(sketch, "E98.2.0.34", {"start": v(1605, -46.06) * mm, "end": v(1693, -46.06) * mm, "construction": true});
            skLineSegment(sketch, "E98.2.0.35", {"start": v(1528, -46.56) * mm, "end": v(1528, -71.56) * mm});
            skLineSegment(sketch, "E98.2.0.36", {"start": v(1234, -67.81) * mm, "end": v(1312, -67.81) * mm, "construction": true});
            skLineSegment(sketch, "E98.2.0.37", {"start": v(1152, -46.56) * mm, "end": v(1152, -71.56) * mm});
            skLineSegment(sketch, "E98.2.0.38", {"start": v(1218, -50.31) * mm, "end": v(1140, -50.31) * mm, "construction": true});
            skLineSegment(sketch, "E98.2.0.39", {"start": v(1414, -41.56) * mm, "end": v(1414, -76.56) * mm, "construction": true});
            skLineSegment(sketch, "E98.2.0.40", {"start": v(1218, -67.81) * mm, "end": v(1140, -67.81) * mm, "construction": true});
            skLineSegment(sketch, "E98.2.0.41", {"start": v(1594, -50.31) * mm, "end": v(1516, -50.31) * mm, "construction": true});
            skPoint(sketch, "E98.2.0.42", {"position": v(1364, -59.06) * mm});
            skLineSegment(sketch, "E98.2.0.43", {"start": v(1312, -50.31) * mm, "end": v(1312, -67.81) * mm, "construction": true});
            skLineSegment(sketch, "E98.2.0.44", {"start": v(1317, -76.56) * mm, "end": v(1411, -76.56) * mm, "construction": true});
            skLineSegment(sketch, "E98.2.0.45", {"start": v(1429, -47.06) * mm, "end": v(1429, -71.06) * mm, "construction": true});
            skPoint(sketch, "E98.2.0.46", {"position": v(1555, -59.06) * mm});
            skLineSegment(sketch, "E98.2.0.47", {"start": v(1429, -47.06) * mm, "end": v(1499, -47.06) * mm, "construction": true});
            skPoint(sketch, "E98.2.0.48", {"position": v(1464, -59.06) * mm});
            skPoint(sketch, "E98.2.0.49", {"position": v(1179, -59.06) * mm});
            skLineSegment(sketch, "E98.2.0.50", {"start": v(1399, -47.06) * mm, "end": v(1329, -47.06) * mm, "construction": true});
            skLineSegment(sketch, "E98.2.0.51", {"start": v(1605, -46.06) * mm, "end": v(1605, -72.06) * mm, "construction": true});
            skLineSegment(sketch, "E98.2.0.52", {"start": v(1317, -41.56) * mm, "end": v(1411, -41.56) * mm, "construction": true});
            skLineSegment(sketch, "E98.2.0.53", {"start": v(1511, -76.56) * mm, "end": v(1417, -76.56) * mm, "construction": true});
            skLineSegment(sketch, "E98.2.0.54", {"start": v(1140, -50.31) * mm, "end": v(1140, -67.81) * mm, "construction": true});
            skLineSegment(sketch, "E98.2.0.55", {"start": v(1516, -50.31) * mm, "end": v(1516, -67.81) * mm, "construction": true});
            skLineSegment(sketch, "E98.2.0.56", {"start": v(1218, -50.31) * mm, "end": v(1218, -67.81) * mm, "construction": true});
            skLineSegment(sketch, "E98.2.0.57", {"start": v(1229, -46.06) * mm, "end": v(1317, -46.06) * mm, "construction": true});
            skLineSegment(sketch, "E98.2.0.58", {"start": v(1437, -46.56) * mm, "end": v(1437, -71.56) * mm});
            skLineSegment(sketch, "E98.2.0.59", {"start": v(1676, -46.56) * mm, "end": v(1676, -71.56) * mm});
            skLineSegment(sketch, "E98.2.0.60", {"start": v(1693, -46.06) * mm, "end": v(1693, -72.06) * mm, "construction": true});
            skLineSegment(sketch, "E98.2.0.61", {"start": v(1511, -41.56) * mm, "end": v(1511, -76.56) * mm, "construction": true});
            skLineSegment(sketch, "E98.2.0.62", {"start": v(1246, -46.56) * mm, "end": v(1246, -71.56) * mm});
            skLineSegment(sketch, "E98.2.0.63", {"start": v(1417, -41.56) * mm, "end": v(1417, -76.56) * mm, "construction": true});
            skLineSegment(sketch, "E98.2.0.64", {"start": v(1226, -46.06) * mm, "end": v(1226, -72.06) * mm, "construction": true});
            skLineSegment(sketch, "E98.2.0.65", {"start": v(1317, -41.56) * mm, "end": v(1317, -76.56) * mm, "construction": true});
            skLineSegment(sketch, "E98.2.0.66", {"start": v(1622, -71.56) * mm, "end": v(1676, -71.56) * mm});
            skPoint(sketch, "E98.2.0.67", {"position": v(1128, -59.06) * mm});
            skLineSegment(sketch, "E98.2.0.68", {"start": v(1411, -41.56) * mm, "end": v(1411, -76.56) * mm, "construction": true});
            skPoint(sketch, "E98.2.0.69", {"position": v(1273, -59.06) * mm});
            skPoint(sketch, "E98.2.0.70", {"position": v(1464, -59.06) * mm});
            skLineSegment(sketch, "E98.2.0.71", {"start": v(1206, -71.56) * mm, "end": v(1152, -71.56) * mm});
            skLineSegment(sketch, "E98.2.0.72", {"start": v(1622, -46.56) * mm, "end": v(1676, -46.56) * mm});
            skLineSegment(sketch, "E98.2.0.73", {"start": v(1391, -71.56) * mm, "end": v(1337, -71.56) * mm});
            skLineSegment(sketch, "E98.2.0.74", {"start": v(1528, -46.56) * mm, "end": v(1582, -46.56) * mm});
            skPoint(sketch, "E98.2.0.75", {"position": v(1649, -59.06) * mm});
            skPoint(sketch, "E98.2.0.76", {"position": v(1555, -59.06) * mm});
            skLineSegment(sketch, "E98.2.0.77", {"start": v(1417, -41.56) * mm, "end": v(1417, -76.56) * mm, "construction": true});
            skLineSegment(sketch, "E98.2.0.78", {"start": v(1511, -46.06) * mm, "end": v(1511, -72.06) * mm, "construction": true});
            skLineSegment(sketch, "E98.2.0.79", {"start": v(1437, -46.56) * mm, "end": v(1491, -46.56) * mm});
            skLineSegment(sketch, "E98.2.0.80", {"start": v(1528, -71.56) * mm, "end": v(1582, -71.56) * mm});
            skLineSegment(sketch, "E98.2.0.81", {"start": v(1300, -46.56) * mm, "end": v(1300, -71.56) * mm});
            skLineSegment(sketch, "E98.2.0.82", {"start": v(1437, -71.56) * mm, "end": v(1491, -71.56) * mm});
            skLineSegment(sketch, "E98.2.0.83", {"start": v(1300, -71.56) * mm, "end": v(1246, -71.56) * mm});
            skLineSegment(sketch, "E98.2.0.84", {"start": v(1391, -46.56) * mm, "end": v(1337, -46.56) * mm});
            skLineSegment(sketch, "E98.2.0.85", {"start": v(1206, -46.56) * mm, "end": v(1152, -46.56) * mm});
            skLineSegment(sketch, "E98.2.0.86", {"start": v(1300, -46.56) * mm, "end": v(1246, -46.56) * mm});
            skPoint(sketch, "E98.2.0.87", {"position": v(1364, -59.06) * mm});
            skPoint(sketch, "E98.2.0.88", {"position": v(1179, -59.06) * mm});
            skPoint(sketch, "E98.2.0.89", {"position": v(1364, -59.06) * mm});
            skPoint(sketch, "E98.2.0.90", {"position": v(1649, -59.06) * mm});
            skLineSegment(sketch, "E98.2.0.91", {"start": v(1135, -46.06) * mm, "end": v(1135, -72.06) * mm, "construction": true});
            skPoint(sketch, "E98.2.0.92", {"position": v(1273, -59.06) * mm});
            skPoint(sketch, "E98.2.0.93", {"position": v(1179, -59.06) * mm});
            skPoint(sketch, "E98.2.0.94", {"position": v(1464, -59.06) * mm});
            skPoint(sketch, "E98.2.0.95", {"position": v(1555, -59.06) * mm});
            skLineSegment(sketch, "E98.2.0.96", {"start": v(1229, -46.06) * mm, "end": v(1226, -46.06) * mm, "construction": true});
            skCircle(sketch, "E98.2.0.97", {"center": v(1234, -50.31) * mm, "radius": 2 * mm});
            skCircle(sketch, "E98.2.0.98", {"center": v(1429, -71.06) * mm, "radius": 2 * mm});
            skCircle(sketch, "E98.2.0.99", {"center": v(1499, -71.06) * mm, "radius": 2 * mm});
            skLineSegment(sketch, "E98.2.0.100", {"start": v(1605, -46.06) * mm, "end": v(1602, -46.06) * mm, "construction": true});
            skCircle(sketch, "E98.2.0.101", {"center": v(1312, -67.81) * mm, "radius": 2 * mm});
            skCircle(sketch, "E98.2.0.102", {"center": v(1610, -67.81) * mm, "radius": 2 * mm});
            skLineSegment(sketch, "E98.2.0.103", {"start": v(1223, -46.06) * mm, "end": v(1226, -46.06) * mm, "construction": true});
            skCircle(sketch, "E98.2.0.104", {"center": v(1218, -67.81) * mm, "radius": 2 * mm});
            skCircle(sketch, "E98.2.0.105", {"center": v(1516, -50.31) * mm, "radius": 2 * mm});
            skCircle(sketch, "E98.2.0.106", {"center": v(1140, -67.81) * mm, "radius": 2 * mm});
            skCircle(sketch, "E98.2.0.107", {"center": v(1218, -50.31) * mm, "radius": 2 * mm});
            skCircle(sketch, "E98.2.0.108", {"center": v(1234, -67.81) * mm, "radius": 2 * mm});
            skCircle(sketch, "E98.2.0.109", {"center": v(1594, -50.31) * mm, "radius": 2 * mm});
            skCircle(sketch, "E98.2.0.110", {"center": v(1329, -71.06) * mm, "radius": 2 * mm});
            skCircle(sketch, "E98.2.0.111", {"center": v(1329, -47.06) * mm, "radius": 2 * mm});
            skCircle(sketch, "E98.2.0.112", {"center": v(1429, -47.06) * mm, "radius": 2 * mm});
            skCircle(sketch, "E98.2.0.113", {"center": v(1610, -50.31) * mm, "radius": 2 * mm});
            skCircle(sketch, "E98.2.0.114", {"center": v(1516, -67.81) * mm, "radius": 2 * mm});
            skCircle(sketch, "E98.2.0.115", {"center": v(1594, -67.81) * mm, "radius": 2 * mm});
            skCircle(sketch, "E98.2.0.116", {"center": v(1140, -50.31) * mm, "radius": 2 * mm});
            skLineSegment(sketch, "E98.2.0.117", {"start": v(1599, -46.06) * mm, "end": v(1602, -46.06) * mm, "construction": true});
            skCircle(sketch, "E98.2.0.118", {"center": v(1688, -67.81) * mm, "radius": 2 * mm});
            skCircle(sketch, "E98.2.0.119", {"center": v(1399, -71.06) * mm, "radius": 2 * mm});
            skCircle(sketch, "E98.2.0.120", {"center": v(1399, -47.06) * mm, "radius": 2 * mm});
            skCircle(sketch, "E98.2.0.121", {"center": v(1499, -47.06) * mm, "radius": 2 * mm});
            skCircle(sketch, "E98.2.0.122", {"center": v(1688, -50.31) * mm, "radius": 2 * mm});
            skCircle(sketch, "E98.2.0.123", {"center": v(1312, -50.31) * mm, "radius": 2 * mm});
            skLineSegment(sketch, "E98.2.0.124", {"start": v(1229, -72.06) * mm, "end": v(1226, -72.06) * mm, "construction": true});
            skLineSegment(sketch, "E98.2.0.125", {"start": v(1599, -72.06) * mm, "end": v(1602, -72.06) * mm, "construction": true});
            skLineSegment(sketch, "E98.2.0.126", {"start": v(1417, -41.56) * mm, "end": v(1414, -41.56) * mm, "construction": true});
            skLineSegment(sketch, "E98.2.0.127", {"start": v(1605, -72.06) * mm, "end": v(1602, -72.06) * mm, "construction": true});
            skLineSegment(sketch, "E98.2.0.128", {"start": v(1417, -76.56) * mm, "end": v(1414, -76.56) * mm, "construction": true});
            skLineSegment(sketch, "E98.2.0.129", {"start": v(1223, -72.06) * mm, "end": v(1226, -72.06) * mm, "construction": true});
            skLineSegment(sketch, "E98.2.0.130", {"start": v(1411, -76.56) * mm, "end": v(1414, -76.56) * mm, "construction": true});
            skLineSegment(sketch, "E98.2.0.131", {"start": v(1411, -41.56) * mm, "end": v(1414, -41.56) * mm, "construction": true});
            skLineSegment(sketch, "E98.direction1", {"start": v(7, -72.06) * mm, "end": v(571, -72.06) * mm, "construction": true});
            skSolve(sketch);
        }
        {
            var Q0;
            Q0=makeQuery(id+"F2.imprint","IMPRINT",FACE,{"disambiguationData":[TD([[makeQuery(id+"F2.imprint","IMPRINT",EDGE,{"derivedFrom":sQuery(id+"F2.wireOp",EDGE,"E6.bottom")}),-1.0]])]});
            extrude(context, id + "F3", {"entities" : qUnion([Q0]), "depth" : 25 * mm});
        }
    });
